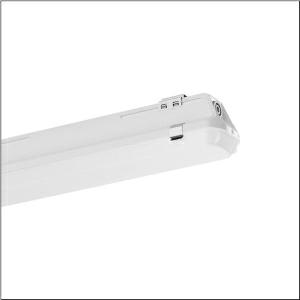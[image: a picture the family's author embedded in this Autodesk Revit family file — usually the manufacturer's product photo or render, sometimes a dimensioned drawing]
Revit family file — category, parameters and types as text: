
# Revit family: monsun_r__11_51fp12mp4b0q_eb41
name_source: partatom
category: Lighting Fixtures
units: mm (PartAtom-declared; Revit-internal decimal feet)

## family parameters
Cut with Voids When Loaded = No
Host = Face
Light Source = No
Part Type = Normal
Room Calculation Point = No
Round Connector Dimension = Use Diameter
Shared = No

## types (1)
- --- (1 x LED, 11850 lm, 66.2 W, 4000K)
    Apparent Load = 66 VA
    CIE Flux Codes = 62 86 96 97 100
    Color Rendering = 80
    Color Temperature = 4000K
    Default Elevation = 1800 mm
    Description = Monsun® 11, damp-proof luminaire, chain hanger, primary light control with lens, primary optical cover: enclosure, of PMMA, light emission: direct distribution, primary light characteristic: symmetric, installation type: suspended mounting, surface-mounted, horizontal mounting, vertical mounting, LED, rated luminous flux: 11.850lm, luminous efficacy: 179lm/W, light colour: 840, colour temperature: 4000K, control gear: ECG, with terminal, 3-pole, max. 2.5mm², mains connection: 220..240V, AC, 50/60Hz, rated input power: 66W, luminaire housing, of glass-fibre reinforced polyester, uncoated, bright grey, incl. chain hanger, length: 1.590mm, width: 90mm, height: 88mm, clip for enclosure, of stainless steel (V2A), ceiling mounting element, of stainless steel (V2A), chain hanger, of stainless steel (V2A), protection rating (complete): IP66, insulation class (complete): insulation class I (protective earthing), certification: CE, ENEC, VDE, UKCA, protection symbol: D, impact resistance: IK04, permissible operating ambient temperature: -35..+35°C, standard: EN 50419, EN 60598-2-1, no direct snow, no direct sun, no direct rain, for indoor or canopied outdoor use, corresponds to IFS (International Featured Standards) requirements for safety and quality in the food industry, contact your sales advisor before using the luminaires in applications with unclear chemical exposure, large temperature fluctuations or condensation-forming humidity, LABS conformity tested according to VDMA 24364:2018-05, packaging unit: 1 piece
    Height = 89 mm
    Lamp = 1 x LED
    Lamp Light Flux = 11850 lm
    Lamp Power = 66.2 W
    Lamp count = 1
    Length = 1590 mm
    Luminous efficacy = 179 lm/W
    Manufacturer = Siteco
    ModVariant = No
    Model = 51FP12MP4B0Q
    Mounting Place = Ceiling
    Mounting Type = Surface mounted
    Number of Poles = 1
    OnlyDefault = Yes
    Power Factor = 1
    Product Name = Monsun® 11
    Product group = damp-proof luminaire
    ProductGroupID = 300
    Protection Class = Protection class I
    Protection Degree = IP 66
    RLX_Detail_Level = 1
    RLX_Emergency_Light_Flux = 0 lm
    RLX_Emergency_Type = 0
    RLX_Emergency_Type_DB = No
    RlxData = <blob elided: 89681 chars, md5=3cf1068f>
    Socket = socket
    Standby Power = 0 W
    System Light Flux = 11850 lm
    System Power = 66 W
    Type Comments = factory setting: luminous flux: 100 % | (A | C | E) | 155 mA
    Type Image = l_1004748.jpg
    URL = http://relux.com
    VarID = @adj_142033
    Voltage = 0 V
    Weight = 0.00 kg
    Width = 90 mm

## geometry (parser evidence)
native form markers: Blend x4, Sweep x9
no freeform markers — native parametric forms only
